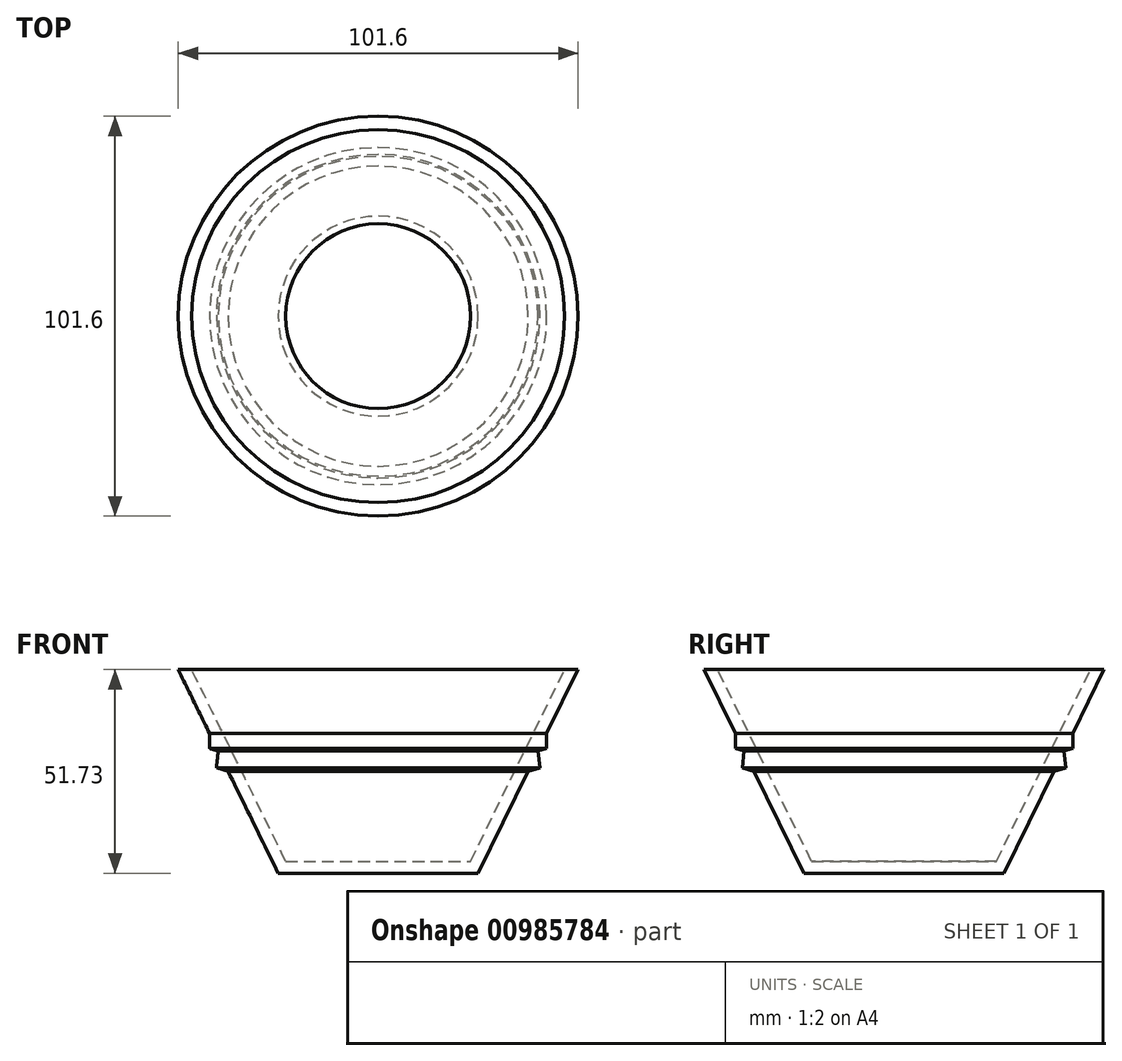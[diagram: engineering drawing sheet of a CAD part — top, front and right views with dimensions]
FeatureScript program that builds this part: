
annotation { "Feature Type Name" : "Feature", "Feature Type Description" : "" }
export const myFeature = defineFeature(function(context is Context, id is Id, definition is map)
    precondition{}
    {
        {
            var Q0;
            Q0=qCreatedBy(makeId("Front.planeOp"),FACE);
            var sketch = newSketch(context, id + "F0", { "sketchPlane" : qUnion([Q0])});
            skLineSegment(sketch, "E0", {"start": v(0, 0) * mm, "end": v(0, 50.8) * mm, "construction": true});
            skLineSegment(sketch, "E1", {"start": v(0, 0) * mm, "end": v(25.4, 0) * mm});
            skLineSegment(sketch, "E2", {"start": v(25.4, 0) * mm, "end": v(50.8, 51.73) * mm});
            skLineSegment(sketch, "E3.0", {"start": v(23.49, 3.07) * mm, "end": v(47.38, 51.73) * mm});
            skLineSegment(sketch, "E3.1", {"start": v(0, 3.07) * mm, "end": v(23.49, 3.07) * mm});
            skLineSegment(sketch, "E4", {"start": v(0, 3.07) * mm, "end": v(0, 0) * mm});
            skLineSegment(sketch, "E5", {"start": v(47.38, 51.73) * mm, "end": v(50.8, 51.73) * mm});
            skLineSegment(sketch, "E6", {"start": v(42.83, 35.5) * mm, "end": v(42.83, 31.7) * mm});
            skLineSegment(sketch, "E7", {"start": v(42.83, 31.7) * mm, "end": v(40.64, 31.04) * mm});
            skLineSegment(sketch, "E8", {"start": v(40.64, 31.04) * mm, "end": v(41.1, 26.82) * mm});
            skLineSegment(sketch, "E9", {"start": v(41.1, 26.82) * mm, "end": v(38.13, 25.92) * mm});
            skSolve(sketch);
        }
        {
            var Q0;
            Q0=makeQuery(id+"F0.imprint","IMPRINT",FACE,{"disambiguationData":[TD([[makeQuery(id+"F0.imprint","IMPRINT",EDGE,{"derivedFrom":sQuery(id+"F0.wireOp",EDGE,"E1")}),1.0]])]});
            var Q1;
            {var subQ0=sQuery(id+"F0.wireOp",EDGE,"E6");Q1=makeQuery(id+"F0.imprint","IMPRINT",FACE,{"disambiguationData":[TD([[makeQuery(id+"F0.imprint","IMPRINT",EDGE,{"derivedFrom":subQ0}),-1.0]])]});}
            var Q2;
            {var subQ0=sQuery(id+"F0.wireOp",EDGE,"E8");Q2=makeQuery(id+"F0.imprint","IMPRINT",FACE,{"disambiguationData":[TD([[makeQuery(id+"F0.imprint","IMPRINT",EDGE,{"derivedFrom":subQ0}),-1.0]])]});}
            var Q3;
            Q3=sQuery(id+"F0.wireOp",EDGE,"E0");
            revolve(context, id + "F1", {"surfaceOperationType" : NewSurfaceOperationType.NEW, "entities" : qUnion([Q0, Q1, Q2]), "axis" : qUnion([Q3]), "revolveType" : RevolveType.FULL});
        }
    });
